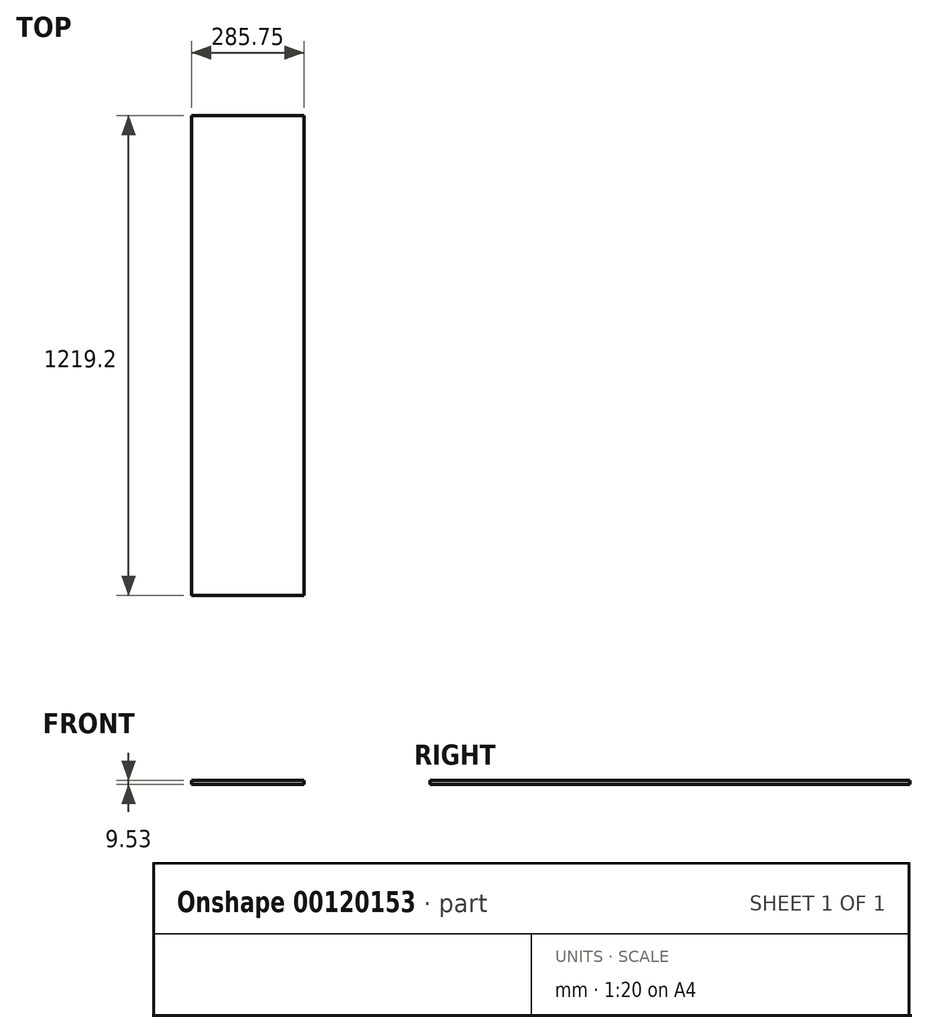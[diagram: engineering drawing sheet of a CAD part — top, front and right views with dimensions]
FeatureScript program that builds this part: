
annotation { "Feature Type Name" : "Feature", "Feature Type Description" : "" }
export const myFeature = defineFeature(function(context is Context, id is Id, definition is map)
    precondition{}
    {
        {
            var Q0;
            Q0=qCreatedBy(makeId("Front.planeOp"),FACE);
            var sketch = newSketch(context, id + "F0", { "sketchPlane" : qUnion([Q0])});
            skLineSegment(sketch, "E0.bottom", {"start": v(0, 0) * mm, "end": v(285.75, 0) * mm});
            skLineSegment(sketch, "E0.top", {"start": v(0, 9.53) * mm, "end": v(285.75, 9.53) * mm});
            skLineSegment(sketch, "E0.left", {"start": v(0, 0) * mm, "end": v(0, 9.53) * mm});
            skLineSegment(sketch, "E0.right", {"start": v(285.75, 0) * mm, "end": v(285.75, 9.53) * mm});
            skSolve(sketch);
        }
        {
            var Q0;
            Q0=makeQuery(id+"F0.imprint","IMPRINT",FACE,{"disambiguationData":[TD([[makeQuery(id+"F0.imprint","IMPRINT",EDGE,{"derivedFrom":sQuery(id+"F0.wireOp",EDGE,"E0.bottom")}),1.0]])]});
            extrude(context, id + "F1", {"entities" : qUnion([Q0]), "depth" : 1219.2 * mm});
        }
    });
